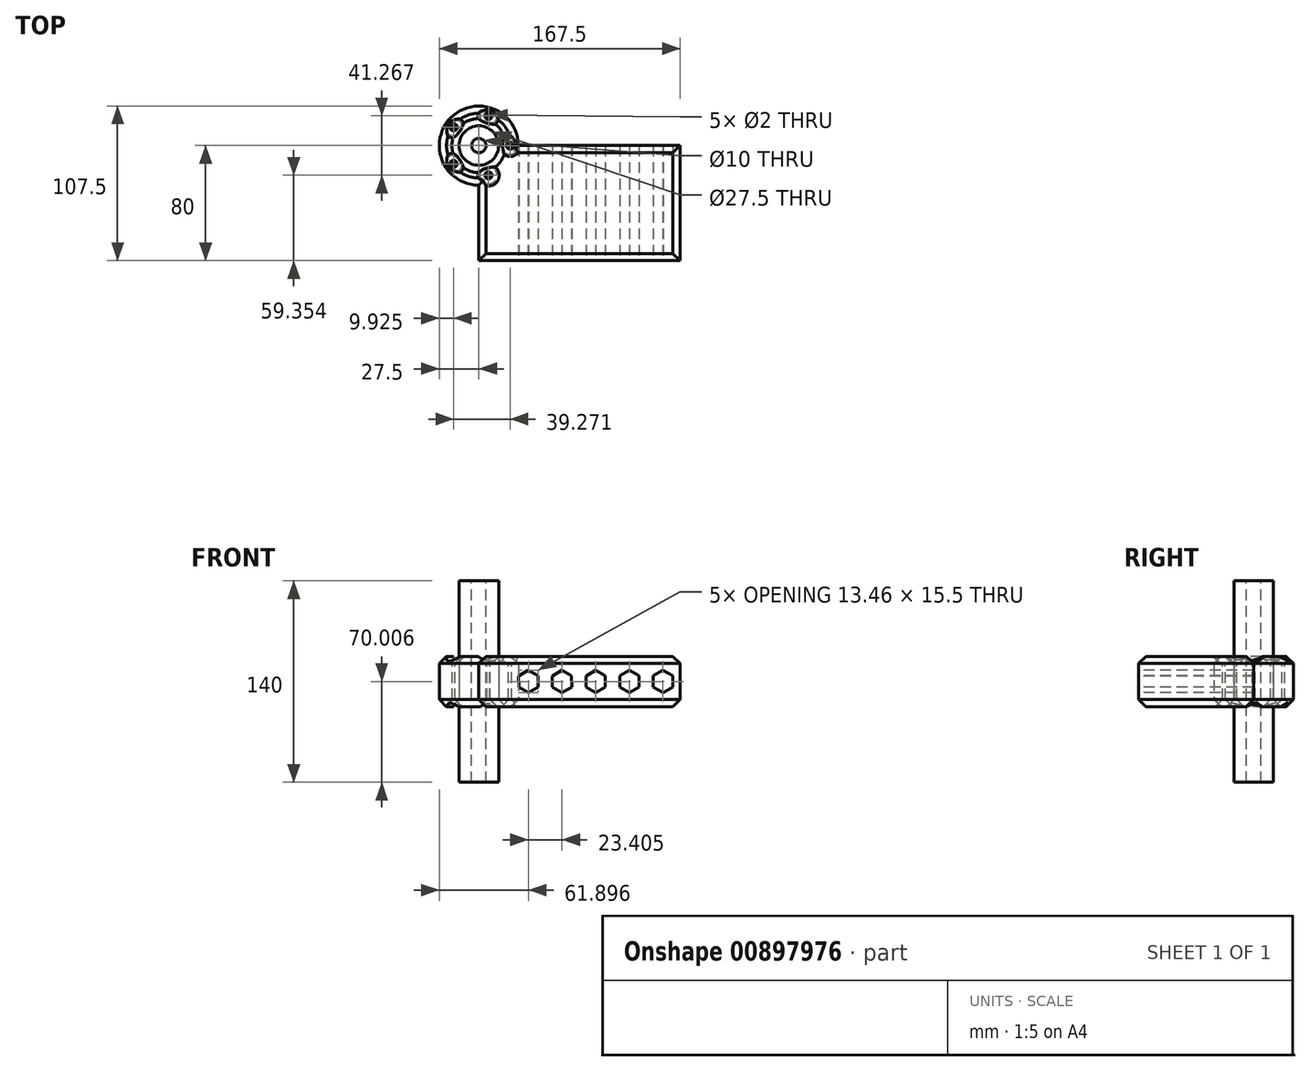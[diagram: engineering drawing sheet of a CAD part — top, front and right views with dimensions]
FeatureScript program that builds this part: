
annotation { "Feature Type Name" : "Feature", "Feature Type Description" : "" }
export const myFeature = defineFeature(function(context is Context, id is Id, definition is map)
    precondition{}
    {
        {
            var Q0;
            Q0=qCreatedBy(makeId("Top.planeOp"),FACE);
            var sketch = newSketch(context, id + "F0", { "sketchPlane" : qUnion([Q0])});
            skLineSegment(sketch, "E0.bottom", {"start": v(70, 40) * mm, "end": v(-70, 40) * mm});
            skLineSegment(sketch, "E0.top", {"start": v(70, -40) * mm, "end": v(-70, -40) * mm});
            skLineSegment(sketch, "E0.left", {"start": v(70, 40) * mm, "end": v(70, -40) * mm});
            skLineSegment(sketch, "E0.right", {"start": v(-70, 40) * mm, "end": v(-70, -40) * mm});
            skPoint(sketch, "E0.middle", {"position": v(0, 0) * mm});
            skCircle(sketch, "E1", {"center": v(-70, 40) * mm, "radius": 27.5 * mm});
            skArc(sketch, "E2", {"start": v(-59.6, 65.46) * mm, "mid": v(3.96, 46.42) * mm, "end": v(70, 40) * mm});
            skCircle(sketch, "E3", {"center": v(-70, 40) * mm, "radius": 13.75 * mm});
            skSolve(sketch);
        }
        {
            var Q0;
            {var subQ0=sQuery(id+"F0.wireOp",EDGE,"E1");var subQ4=sQuery(id+"F0.wireOp",EDGE,"E0.bottom");var subQ5=makeQuery(id+"F0.imprint","INTERSECT",VERTEX,{"derivedFrom":[subQ4,subQ0]});Q0=makeQuery(id+"F0.imprint","IMPRINT",FACE,{"disambiguationData":[TD([[makeQuery(id+"F0.imprint","IMPRINT",EDGE,{"disambiguationData":[TD([[subQ5,-1.0]])],"derivedFrom":subQ4}),-1.0]])]});}
            var Q1;
            {var subQ0=sQuery(id+"F0.wireOp",EDGE,"E1");var subQ1=sQuery(id+"F0.wireOp",EDGE,"E0.bottom");var subQ2=makeQuery(id+"F0.imprint","INTERSECT",VERTEX,{"derivedFrom":[subQ1,subQ0]});Q1=makeQuery(id+"F0.imprint","IMPRINT",FACE,{"disambiguationData":[TD([[makeQuery(id+"F0.imprint","IMPRINT",EDGE,{"disambiguationData":[TD([[subQ2,-1.0]])],"derivedFrom":subQ1}),1.0]])]});}
            var Q2;
            {var subQ1=sQuery(id+"F0.wireOp",EDGE,"E0.top");Q2=makeQuery(id+"F0.imprint","IMPRINT",FACE,{"disambiguationData":[TD([[makeQuery(id+"F0.imprint","IMPRINT",EDGE,{"derivedFrom":subQ1}),-1.0]])]});}
            extrude(context, id + "F1", {"entities" : qUnion([Q0, Q1, Q2]), "endBound" : BoundingType.SYMMETRIC, "depth" : 35 * mm, "offsetDistance" : 25 * mm});
        }
        {
            var Q0;
            {var subQ0=sQuery(id+"F0.wireOp",EDGE,"E0.right");var subQ1=sQuery(id+"F0.wireOp",EDGE,"E0.bottom");var subQ2=makeQuery(id+"F0.imprint","INTERSECT",VERTEX,{"derivedFrom":[subQ1,subQ0]});Q0=makeQuery(id+"F0.imprint","IMPRINT",FACE,{"disambiguationData":[TD([[makeQuery(id+"F0.imprint","IMPRINT",EDGE,{"disambiguationData":[TD([[subQ2,1.0]])],"derivedFrom":subQ1}),-1.0]])]});}
            var Q1;
            {var subQ0=sQuery(id+"F0.wireOp",EDGE,"E0.right");var subQ1=sQuery(id+"F0.wireOp",EDGE,"E0.bottom");var subQ2=makeQuery(id+"F0.imprint","INTERSECT",VERTEX,{"derivedFrom":[subQ1,subQ0]});Q1=makeQuery(id+"F0.imprint","IMPRINT",FACE,{"disambiguationData":[TD([[makeQuery(id+"F0.imprint","IMPRINT",EDGE,{"disambiguationData":[TD([[subQ2,1.0]])],"derivedFrom":subQ1}),1.0]])]});}
            extrude(context, id + "F2", {"entities" : qUnion([Q0, Q1]), "endBound" : BoundingType.SYMMETRIC, "depth" : 140 * mm, "offsetDistance" : 25 * mm});
        }
        {
            var Q0;
            Q0=makeQuery(id+"F1.opExtrude","SWEPT_FACE",FACE,{"disambiguationData":[OSD([sQuery(id+"F0.wireOp",EDGE,"E0.top")])]});
            var sketch = newSketch(context, id + "F3", { "sketchPlane" : qUnion([Q0])});
            skLineSegment(sketch, "E4.1.0.0", {"start": v(-28.9, 3.91) * mm, "end": v(-28.87, -3.84) * mm});
            skLineSegment(sketch, "E4.1.0.1", {"start": v(-42.3, -3.9) * mm, "end": v(-42.33, 3.85) * mm});
            skLineSegment(sketch, "E4.1.0.2", {"start": v(-42.33, 3.85) * mm, "end": v(-35.64, 7.76) * mm});
            skLineSegment(sketch, "E4.1.0.3", {"start": v(-28.87, -3.84) * mm, "end": v(-35.57, -7.75) * mm});
            skLineSegment(sketch, "E4.1.0.4", {"start": v(-35.57, -7.75) * mm, "end": v(-42.3, -3.9) * mm});
            skCircle(sketch, "E4.1.0.5", {"center": v(-35.6, 0) * mm, "radius": 7.75 * mm, "construction": true});
            skLineSegment(sketch, "E4.1.0.6", {"start": v(-35.64, 7.76) * mm, "end": v(-28.9, 3.91) * mm});
            skLineSegment(sketch, "E4.2.0.0", {"start": v(-5.5, 3.92) * mm, "end": v(-5.47, -3.83) * mm});
            skLineSegment(sketch, "E4.2.0.1", {"start": v(-18.9, -3.9) * mm, "end": v(-18.93, 3.86) * mm});
            skLineSegment(sketch, "E4.2.0.2", {"start": v(-18.93, 3.86) * mm, "end": v(-12.23, 7.76) * mm});
            skLineSegment(sketch, "E4.2.0.3", {"start": v(-5.47, -3.83) * mm, "end": v(-12.16, -7.74) * mm});
            skLineSegment(sketch, "E4.2.0.4", {"start": v(-12.16, -7.74) * mm, "end": v(-18.9, -3.9) * mm});
            skCircle(sketch, "E4.2.0.5", {"center": v(-12.2, 0.01) * mm, "radius": 7.75 * mm, "construction": true});
            skLineSegment(sketch, "E4.2.0.6", {"start": v(-12.23, 7.76) * mm, "end": v(-5.5, 3.92) * mm});
            skLineSegment(sketch, "E4.3.0.0", {"start": v(17.9, 3.92) * mm, "end": v(17.94, -3.83) * mm});
            skLineSegment(sketch, "E4.3.0.1", {"start": v(4.51, -3.89) * mm, "end": v(4.48, 3.86) * mm});
            skLineSegment(sketch, "E4.3.0.2", {"start": v(4.48, 3.86) * mm, "end": v(11.17, 7.77) * mm});
            skLineSegment(sketch, "E4.3.0.3", {"start": v(17.94, -3.83) * mm, "end": v(11.24, -7.73) * mm});
            skLineSegment(sketch, "E4.3.0.4", {"start": v(11.24, -7.73) * mm, "end": v(4.51, -3.89) * mm});
            skCircle(sketch, "E4.3.0.5", {"center": v(11.2, 0.02) * mm, "radius": 7.75 * mm, "construction": true});
            skLineSegment(sketch, "E4.3.0.6", {"start": v(11.17, 7.77) * mm, "end": v(17.9, 3.92) * mm});
            skLineSegment(sketch, "E4.4.0.0", {"start": v(41.3, 3.93) * mm, "end": v(41.34, -3.82) * mm});
            skLineSegment(sketch, "E4.4.0.1", {"start": v(27.92, -3.88) * mm, "end": v(27.88, 3.87) * mm});
            skLineSegment(sketch, "E4.4.0.2", {"start": v(27.88, 3.87) * mm, "end": v(34.58, 7.77) * mm});
            skLineSegment(sketch, "E4.4.0.3", {"start": v(41.34, -3.82) * mm, "end": v(34.65, -7.73) * mm});
            skLineSegment(sketch, "E4.4.0.4", {"start": v(34.65, -7.73) * mm, "end": v(27.92, -3.88) * mm});
            skCircle(sketch, "E4.4.0.5", {"center": v(34.61, 0.02) * mm, "radius": 7.75 * mm, "construction": true});
            skLineSegment(sketch, "E4.4.0.6", {"start": v(34.58, 7.77) * mm, "end": v(41.3, 3.93) * mm});
            skLineSegment(sketch, "E4.direction1", {"start": v(-65.7, -3.9) * mm, "end": v(-42.3, -3.9) * mm, "construction": true});
            skLineSegment(sketch, "E5.0.5.0", {"start": v(64.71, 3.93) * mm, "end": v(64.75, -3.82) * mm});
            skLineSegment(sketch, "E5.3.5.0", {"start": v(51.32, -3.88) * mm, "end": v(51.29, 3.87) * mm});
            skLineSegment(sketch, "E5.6.5.0", {"start": v(51.29, 3.87) * mm, "end": v(57.98, 7.78) * mm});
            skLineSegment(sketch, "E5.9.5.0", {"start": v(64.75, -3.82) * mm, "end": v(58.05, -7.72) * mm});
            skLineSegment(sketch, "E5.12.5.0", {"start": v(58.05, -7.72) * mm, "end": v(51.32, -3.88) * mm});
            skCircle(sketch, "E5.15.5.0", {"center": v(58.02, 0.03) * mm, "radius": 7.75 * mm, "construction": true});
            skLineSegment(sketch, "E5.17.5.0", {"start": v(57.98, 7.78) * mm, "end": v(64.71, 3.93) * mm});
            skSolve(sketch);
        }
        {
            var Q0;
            Q0=makeQuery(id+"F3.imprint","IMPRINT",FACE,{"disambiguationData":[TD([[makeQuery(id+"F3.imprint","IMPRINT",EDGE,{"derivedFrom":sQuery(id+"F3.wireOp",EDGE,"E4.2.0.0")}),-1.0]])]});
            var Q1;
            Q1=makeQuery(id+"F3.imprint","IMPRINT",FACE,{"disambiguationData":[TD([[makeQuery(id+"F3.imprint","IMPRINT",EDGE,{"derivedFrom":sQuery(id+"F3.wireOp",EDGE,"629380d3-7284-4796-a378-ed9a0590a229.0")}),-1.0]])]});
            var Q2;
            Q2=makeQuery(id+"F3.imprint","IMPRINT",FACE,{"disambiguationData":[TD([[makeQuery(id+"F3.imprint","IMPRINT",EDGE,{"derivedFrom":sQuery(id+"F3.wireOp",EDGE,"E4.1.0.0")}),-1.0]])]});
            var Q3;
            Q3=makeQuery(id+"F3.imprint","IMPRINT",FACE,{"disambiguationData":[TD([[makeQuery(id+"F3.imprint","IMPRINT",EDGE,{"derivedFrom":sQuery(id+"F3.wireOp",EDGE,"E4.4.0.0")}),-1.0]])]});
            var Q4;
            Q4=makeQuery(id+"F3.imprint","IMPRINT",FACE,{"disambiguationData":[TD([[makeQuery(id+"F3.imprint","IMPRINT",EDGE,{"derivedFrom":sQuery(id+"F3.wireOp",EDGE,"E5.0.5.0")}),-1.0]])]});
            var Q5;
            Q5=makeQuery(id+"F3.imprint","IMPRINT",FACE,{"disambiguationData":[TD([[makeQuery(id+"F3.imprint","IMPRINT",EDGE,{"derivedFrom":sQuery(id+"F3.wireOp",EDGE,"E4.3.0.0")}),-1.0]])]});
            extrude(context, id + "F4", {"entities" : qUnion([Q0, Q1, Q2, Q3, Q4, Q5]), "operationType" : NewBodyOperationType.REMOVE, "endBound" : BoundingType.SYMMETRIC, "oppositeDirection" : true, "depth" : 205 * mm, "offsetDistance" : 25 * mm});
        }
        {
            var Q0;
            Q0=makeQuery(id+"F1.opExtrude","CAP_FACE",FACE,{"disambiguationData":[OSD([sQuery(id+"F0.wireOp",EDGE,"E0.bottom"),sQuery(id+"F0.wireOp",EDGE,"E0.top"),sQuery(id+"F0.wireOp",EDGE,"E0.left"),sQuery(id+"F0.wireOp",EDGE,"E0.right"),sQuery(id+"F0.wireOp",EDGE,"E1"),sQuery(id+"F0.wireOp",EDGE,"E3")])],"isStart":false});
            var sketch = newSketch(context, id + "F5", { "sketchPlane" : qUnion([Q0])});
            skPoint(sketch, "E6", {"position": v(-48.3, 39.96) * mm});
            skPoint(sketch, "E7.1.0", {"position": v(-63.26, 60.62) * mm});
            skPoint(sketch, "E7.2.0", {"position": v(-87.53, 52.78) * mm});
            skPoint(sketch, "E7.3.0", {"position": v(-87.58, 27.28) * mm});
            skPoint(sketch, "E7.4.0", {"position": v(-63.33, 19.35) * mm});
            skPoint(sketch, "E7.center", {"position": v(-70, 40) * mm});
            skSolve(sketch);
        }
        {
            var Q0;
            Q0=sQuery(id+"F5.wireOp",VERTEX,"E7.2.0");
            var Q1;
            Q1=sQuery(id+"F5.wireOp",VERTEX,"E7.3.0");
            var Q2;
            Q2=sQuery(id+"F5.wireOp",VERTEX,"E7.4.0");
            var Q3;
            Q3=sQuery(id+"F5.wireOp",VERTEX,"E6");
            var Q4;
            Q4=sQuery(id+"F5.wireOp",VERTEX,"E7.1.0");
            var Q5;
            Q5=makeQuery(id+"F1.opExtrude","SWEPT_BODY",BODY,{"disambiguationData":[OSD([sQuery(id+"F0.wireOp",EDGE,"E0.bottom"),sQuery(id+"F0.wireOp",EDGE,"E0.top"),sQuery(id+"F0.wireOp",EDGE,"E0.left"),sQuery(id+"F0.wireOp",EDGE,"E0.right"),sQuery(id+"F0.wireOp",EDGE,"E1"),sQuery(id+"F0.wireOp",EDGE,"E3")])]});
            hole(context, id + "F6", {"style" : HoleStyle.C_BORE, "endStyle" : HoleEndStyle.THROUGH, "holeDiameter" : 2 * mm, "cBoreDiameter" : 5 * mm, "cBoreDepth" : 5 * mm, "majorDiameter" : 5 * mm, "isTappedThrough" : true, "tappedDepth" : 12 * mm, "tapClearance" : 3, "locations" : qUnion([Q0, Q1, Q2, Q3, Q4]), "scope" : qUnion([Q5])});
        }
        {
            var Q0;
            Q0=makeQuery(id+"F2.opExtrude","CAP_FACE",FACE,{"disambiguationData":[OSD([sQuery(id+"F0.wireOp",EDGE,"E3")])],"isStart":false});
            var sketch = newSketch(context, id + "F7", { "sketchPlane" : qUnion([Q0])});
            skPoint(sketch, "E8", {"position": v(-70, 40) * mm});
            skSolve(sketch);
        }
        {
            var Q0;
            Q0=sQuery(id+"F7.wireOp",VERTEX,"E8");
            var Q1;
            Q1=makeQuery(id+"F2.opExtrude","SWEPT_BODY",BODY,{"disambiguationData":[OSD([sQuery(id+"F0.wireOp",EDGE,"E3")])]});
            hole(context, id + "F8", {"style" : HoleStyle.C_BORE, "endStyle" : HoleEndStyle.THROUGH, "holeDiameter" : 10 * mm, "cBoreDiameter" : 10 * mm, "cBoreDepth" : 30 * mm, "majorDiameter" : 5 * mm, "isTappedThrough" : true, "tappedDepth" : 12 * mm, "tapClearance" : 3, "locations" : qUnion([Q0]), "scope" : qUnion([Q1])});
        }
        {
            var Q0;
            Q0=makeQuery(id+"F1.opExtrude","CAP_FACE",FACE,{"disambiguationData":[OSD([sQuery(id+"F0.wireOp",EDGE,"E0.bottom"),sQuery(id+"F0.wireOp",EDGE,"E0.top"),sQuery(id+"F0.wireOp",EDGE,"E0.left"),sQuery(id+"F0.wireOp",EDGE,"E0.right"),sQuery(id+"F0.wireOp",EDGE,"E1"),sQuery(id+"F0.wireOp",EDGE,"E3")])],"isStart":false});
            var Q1;
            Q1=makeQuery(id+"F1.opExtrude","CAP_FACE",FACE,{"disambiguationData":[OSD([sQuery(id+"F0.wireOp",EDGE,"E0.bottom"),sQuery(id+"F0.wireOp",EDGE,"E0.top"),sQuery(id+"F0.wireOp",EDGE,"E0.left"),sQuery(id+"F0.wireOp",EDGE,"E0.right"),sQuery(id+"F0.wireOp",EDGE,"E1"),sQuery(id+"F0.wireOp",EDGE,"E3")])],"isStart":true});
            chamfer(context, id + "F9", {"entities" : qUnion([Q0, Q1]), "width" : 5 * mm, "tangentPropagation" : true});
        }
    });
